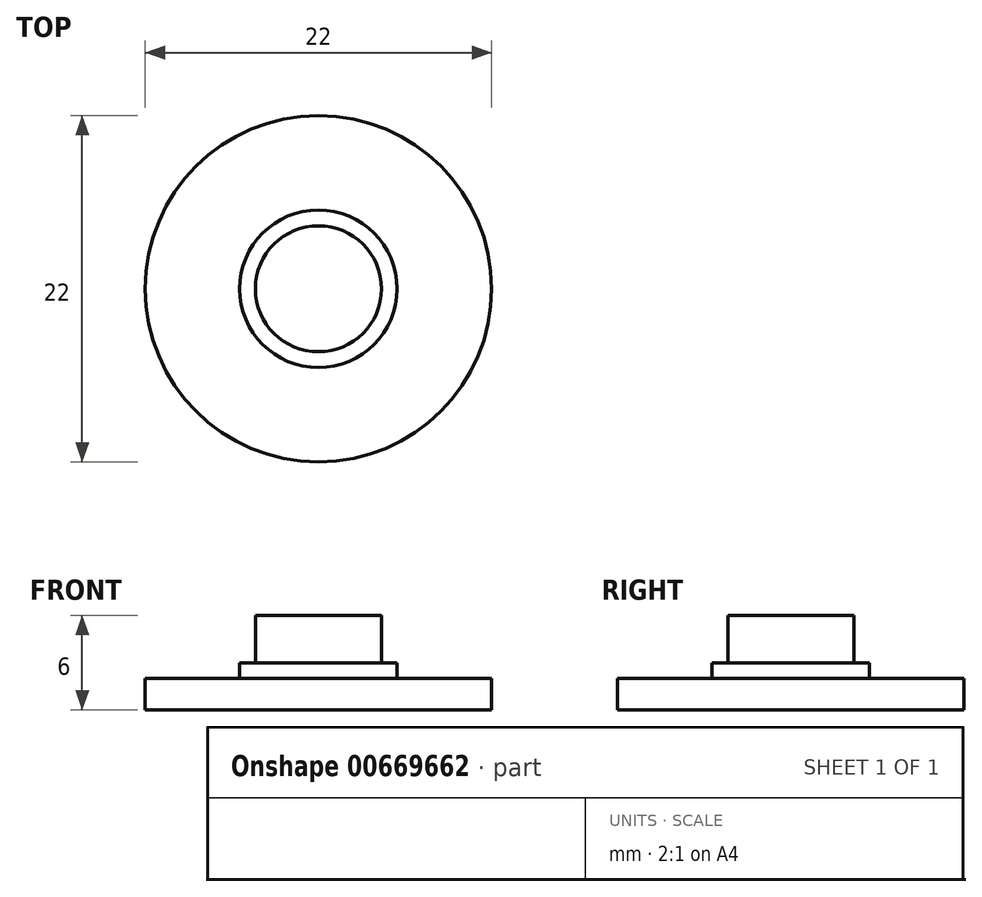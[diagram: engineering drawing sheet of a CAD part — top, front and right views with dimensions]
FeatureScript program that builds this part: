
annotation { "Feature Type Name" : "Feature", "Feature Type Description" : "" }
export const myFeature = defineFeature(function(context is Context, id is Id, definition is map)
    precondition{}
    {
        {
            var Q0;
            Q0=qCreatedBy(makeId("Top.planeOp"),FACE);
            var sketch = newSketch(context, id + "F0", { "sketchPlane" : qUnion([Q0])});
            skCircle(sketch, "E0", {"center": v(0, 0) * mm, "radius": 11 * mm});
            skSolve(sketch);
        }
        {
            var Q0;
            Q0 = qSketchRegion(id + "F0", true);
            var Q1;
            Q1=makeQuery(id+"F0.imprint","IMPRINT",FACE,{"disambiguationData":[TD([[makeQuery(id+"F0.imprint","IMPRINT",EDGE,{"derivedFrom":sQuery(id+"F0.wireOp",EDGE,"E0")}),1.0]])]});
            extrude(context, id + "F1", {"entities" : qUnion([Q0, Q1]), "depth" : 2 * mm, "offsetDistance" : 25 * mm});
        }
        {
            var Q0;
            Q0=makeQuery(id+"F1.opExtrude","CAP_FACE",FACE,{"disambiguationData":[OSD([sQuery(id+"F0.wireOp",EDGE,"E0")])],"isStart":false});
            var sketch = newSketch(context, id + "F2", { "sketchPlane" : qUnion([Q0])});
            skCircle(sketch, "E1", {"center": v(0, 0) * mm, "radius": 5 * mm});
            skSolve(sketch);
        }
        {
            var Q0;
            Q0 = qSketchRegion(id + "F2", true);
            extrude(context, id + "F3", {"entities" : qUnion([Q0]), "operationType" : NewBodyOperationType.ADD, "depth" : 1 * mm, "offsetDistance" : 25 * mm});
        }
        {
            var Q0;
            Q0=makeQuery(id+"F3.opExtrude","CAP_FACE",FACE,{"disambiguationData":[OSD([sQuery(id+"F2.wireOp",EDGE,"E1")])],"isStart":false});
            var sketch = newSketch(context, id + "F4", { "sketchPlane" : qUnion([Q0])});
            skCircle(sketch, "E2", {"center": v(0, 0) * mm, "radius": 4 * mm});
            skSolve(sketch);
        }
        {
            var Q0;
            Q0 = qSketchRegion(id + "F4", true);
            extrude(context, id + "F5", {"entities" : qUnion([Q0]), "operationType" : NewBodyOperationType.ADD, "depth" : 3 * mm, "offsetDistance" : 25 * mm});
        }
    });
